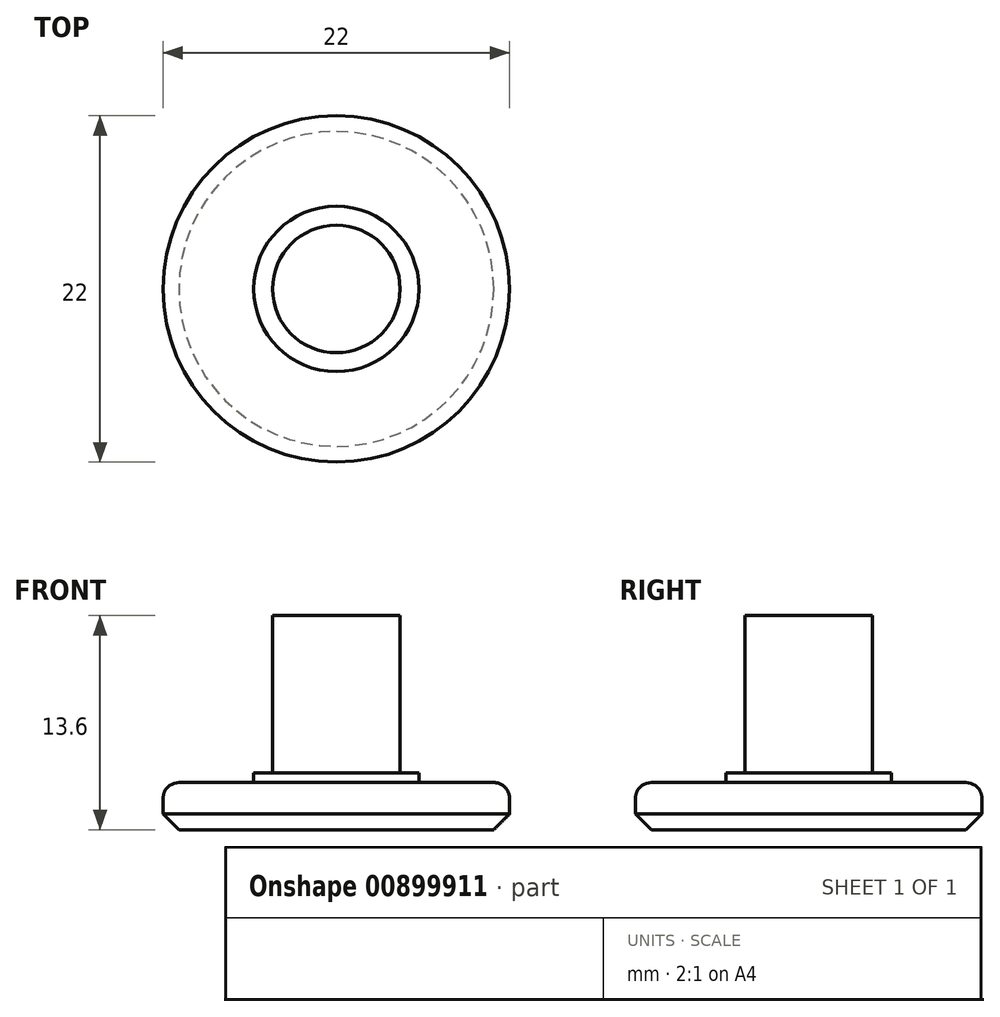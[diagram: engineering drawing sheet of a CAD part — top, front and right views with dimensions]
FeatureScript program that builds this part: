
annotation { "Feature Type Name" : "Feature", "Feature Type Description" : "" }
export const myFeature = defineFeature(function(context is Context, id is Id, definition is map)
    precondition{}
    {
        {
            var Q0;
            Q0=qCreatedBy(makeId("Top.planeOp"),FACE);
            var sketch = newSketch(context, id + "F0", { "sketchPlane" : qUnion([Q0])});
            skCircle(sketch, "E0", {"center": v(0, 0) * mm, "radius": 11 * mm});
            skSolve(sketch);
        }
        {
            var Q0;
            Q0=makeQuery(id+"F0.imprint","IMPRINT",FACE,{"disambiguationData":[TD([[makeQuery(id+"F0.imprint","IMPRINT",EDGE,{"derivedFrom":sQuery(id+"F0.wireOp",EDGE,"E0")}),1.0]])]});
            extrude(context, id + "F1", {"entities" : qUnion([Q0]), "depth" : 3 * mm, "offsetDistance" : 25 * mm});
        }
        {
            var Q0;
            Q0=makeQuery(id+"F1.opExtrude","CAP_FACE",FACE,{"disambiguationData":[OSD([sQuery(id+"F0.wireOp",EDGE,"E0")])],"isStart":false});
            var sketch = newSketch(context, id + "F2", { "sketchPlane" : qUnion([Q0])});
            skCircle(sketch, "E1", {"center": v(0, 0) * mm, "radius": 5.25 * mm});
            skSolve(sketch);
        }
        {
            var Q0;
            Q0=makeQuery(id+"F2.imprint","IMPRINT",FACE,{"disambiguationData":[TD([[makeQuery(id+"F2.imprint","IMPRINT",EDGE,{"derivedFrom":sQuery(id+"F2.wireOp",EDGE,"E1")}),1.0]])]});
            extrude(context, id + "F3", {"entities" : qUnion([Q0]), "operationType" : NewBodyOperationType.ADD, "depth" : .6 * mm, "offsetDistance" : 25 * mm});
        }
        {
            var Q0;
            Q0=makeQuery(id+"F3.opExtrude","CAP_FACE",FACE,{"disambiguationData":[OSD([sQuery(id+"F2.wireOp",EDGE,"E1")])],"isStart":false});
            var sketch = newSketch(context, id + "F4", { "sketchPlane" : qUnion([Q0])});
            skCircle(sketch, "E2", {"center": v(0, 0) * mm, "radius": 4.05 * mm});
            skSolve(sketch);
        }
        {
            var Q0;
            Q0=makeQuery(id+"F4.imprint","IMPRINT",FACE,{"disambiguationData":[TD([[makeQuery(id+"F4.imprint","IMPRINT",EDGE,{"derivedFrom":sQuery(id+"F4.wireOp",EDGE,"E2")}),1.0]])]});
            extrude(context, id + "F5", {"entities" : qUnion([Q0]), "operationType" : NewBodyOperationType.ADD, "depth" : 10 * mm, "offsetDistance" : 25 * mm});
        }
        {
            var Q0;
            Q0=makeQuery(id+"F1.opExtrude","CAP_EDGE",EDGE,{"disambiguationData":[OSD([sQuery(id+"F0.wireOp",EDGE,"E0")])],"isStart":true});
            chamfer(context, id + "F6", {"entities" : qUnion([Q0]), "width" : 1 * mm, "tangentPropagation" : true});
        }
        {
            var Q0;
            Q0=makeQuery(id+"F1.opExtrude","CAP_EDGE",EDGE,{"disambiguationData":[OSD([sQuery(id+"F0.wireOp",EDGE,"E0")])],"isStart":false});
            fillet(context, id + "F7", {"entities" : qUnion([Q0]), "radius" : 1 * mm, "tangentPropagation" : true, "allowEdgeOverflow" : false});
        }
    });
